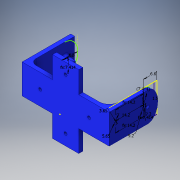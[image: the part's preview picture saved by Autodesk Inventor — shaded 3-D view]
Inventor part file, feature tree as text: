
AUTODESK INVENTOR PART (.ipt)
format: ipt  version: 2016 (Build 200138000, 138)  size: 330,752 bytes
history: native  units: in
note: dims shown in document units (in); Inventor stores cm internally (conversion verified against a paired STEP export)
features: sketch x11, extrude x9, fillet x8, plane x2, hole x2
ambient origin geometry x8: Origin, YZ Plane, XZ Plane, XY Plane, X Axis, Y Axis, Z Axis, Center Point
bodies: Solid1 (feature_tree)
feature tree (32):
  extrude  "Extrusion1"  Depth=0.5838in
  extrude  "Extrusion3"  Depth=0.0787in
  sketch  "Sketch5"  dims[d9=0.9449in d10=0.0in d11=0.2835in d12=0.2598in d13=0.2919in d14=0.2919in d15=0.5838in d16=0.3622in]
  extrude  "Extrusion4"  Depth=0.5838in
  fillet  "Fillet1"  Radius=0.2598in
  fillet  "Fillet4"  Radius=0.2919in
  fillet  "Fillet5"  Radius=0.2919in
  fillet  "Fillet6"  Radius=0.5838in
  fillet  "Fillet7"  Radius=0.3622in
  extrude  "Extrusion6"  Depth=0.2224in
  sketch  "Sketch9"  dims[d17=0.1437in d19=0.2224in]
  extrude  "Extrusion7"  Depth=0.0394in
  fillet  "Fillet10"  Radius=0.0197in
  fillet  "Fillet11"  Radius=0.0394in
  sketch  "Sketch10"  dims[d24=0.0787in d25=0.0in d30=0.1969in d33=0.0197in d34=0.0394in]
  plane  "Work Plane2"
  extrude  "Extrusion10"  Depth=0.0197in
  plane  "Work Plane3"
  extrude  "Extrusion11"  Depth=0.0787in TaperAngle=0.0deg
  sketch  "Sketch17"  dims[d45=0.2598in d46=0.1181in d47=0.1772in d48=0.0in]
  hole  "Hole2"  [1 undecoded]
  fillet  "Fillet18"  Radius=0.1772in
  hole  "Hole3"  [1 undecoded]
  extrude  "Extrusion14"  Depth=0.6043in
  extrude  "Extrusion15"  Depth=0.4291in TaperAngle=0.0deg
  sketch  "Sketch1"  dims[d0=1.7283in d1=0.5838in]
  sketch  "Sketch4"  dims[d2=0.0787in d3=0.0in d8=0.0787in]
  sketch  "Sketch15"  dims[d35=0.0394in d36=0.0197in]
  sketch  "Sketch16"  dims[d37=0.0787in d38=0.9449in d39=0.0in]
  sketch  "Sketch18"  dims[d49=0.0394in d50=0.0197in]
  sketch  "Sketch19"  dims[d82=0.5197in d83=0.6043in]
  sketch  "Sketch20"  dims[d84=0.6043in d85=0.4291in d86=0.0in d87=0.6043in d88=0.4291in d89=0.0in d90=0.0591in d91=0.2362in d92=0.1575in d93=0.0787in d94=90.0deg d95=0.315in d96=0.8108in d98=0.1181in d99=0.5591in d100=0.5591in d101=0.5591in d106=0.0591in d112=0.0591in d113=0.2362in d114=0.1575in d115=0.0787in d116=90.0deg d117=0.315in d118=0.8108in d120=0.5838in d121=0.2919in d122=0.3937in d123=0.0in d124=0.0591in d125=0.0in]
note: 2 required parameter values undecoded (feature->parameter linkage not recoverable at this tier; creation-order binding heuristic only, values carry confidence <= 0.55)
